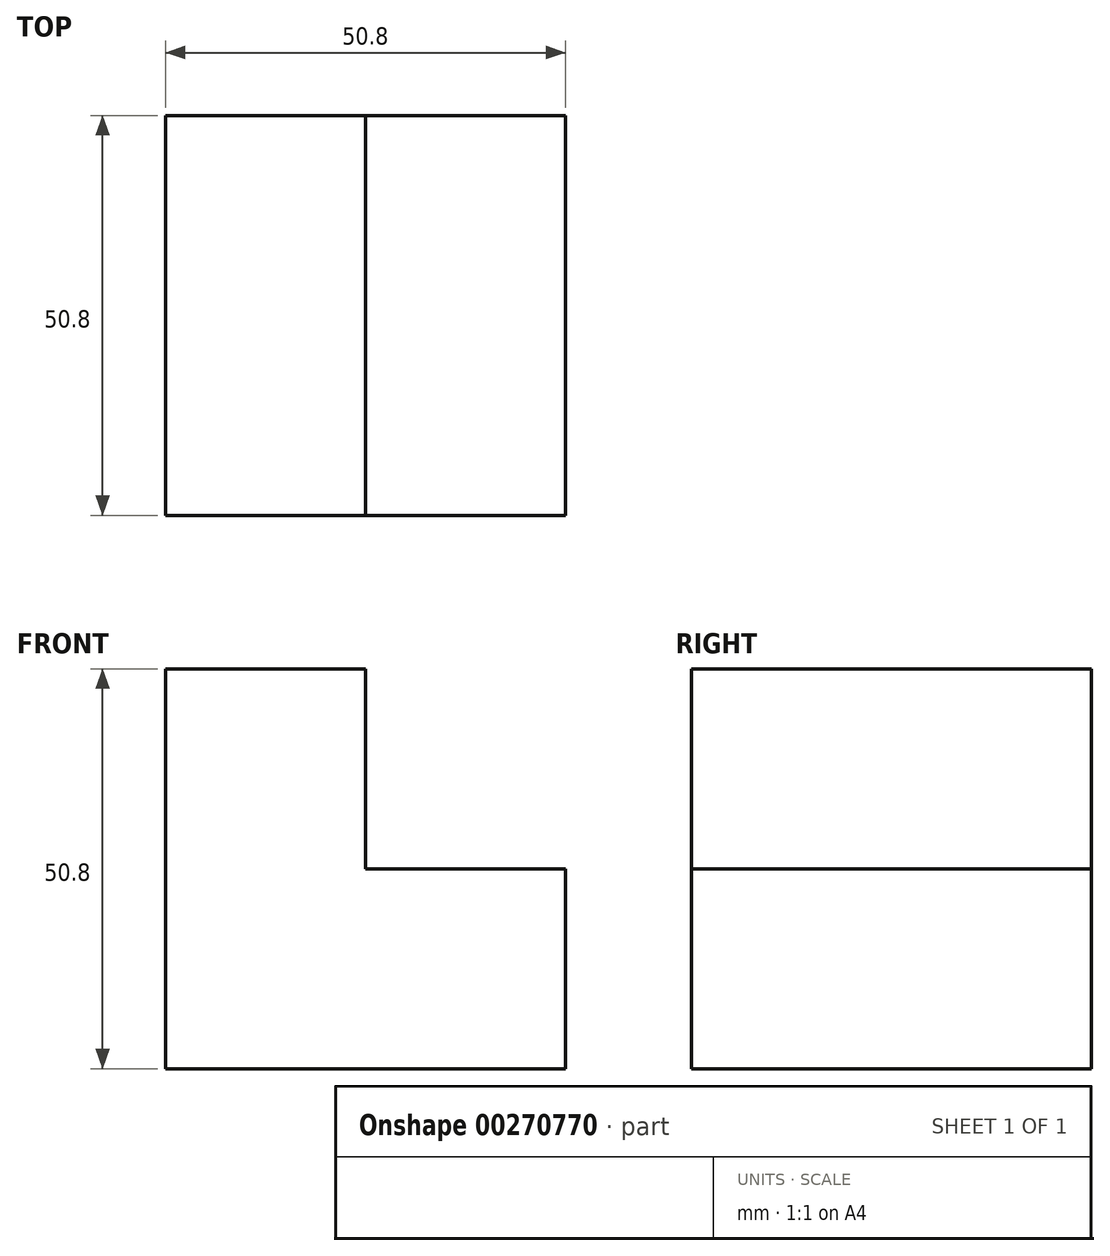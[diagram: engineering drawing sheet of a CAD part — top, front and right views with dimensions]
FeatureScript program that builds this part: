
annotation { "Feature Type Name" : "Feature", "Feature Type Description" : "" }
export const myFeature = defineFeature(function(context is Context, id is Id, definition is map)
    precondition{}
    {
        {
            var Q0;
            Q0=qCreatedBy(makeId("Front.planeOp"),FACE);
            var sketch = newSketch(context, id + "F0", { "sketchPlane" : qUnion([Q0])});
            skLineSegment(sketch, "E0", {"start": v(0, 0) * mm, "end": v(-50.8, 0) * mm});
            skLineSegment(sketch, "E1", {"start": v(-50.8, 0) * mm, "end": v(-50.8, 50.8) * mm});
            skLineSegment(sketch, "E2", {"start": v(-50.8, 50.8) * mm, "end": v(-25.4, 50.8) * mm});
            skLineSegment(sketch, "E3", {"start": v(-25.4, 25.4) * mm, "end": v(-25.4, 50.8) * mm});
            skLineSegment(sketch, "E4", {"start": v(-25.4, 25.4) * mm, "end": v(0, 25.4) * mm});
            skLineSegment(sketch, "E5", {"start": v(0, 0) * mm, "end": v(0, 25.4) * mm});
            skSolve(sketch);
        }
        {
            var Q0;
            Q0 = qSketchRegion(id + "F0", true);
            extrude(context, id + "F1", {"entities" : qUnion([Q0]), "depth" : 50.8 * mm});
        }
    });
